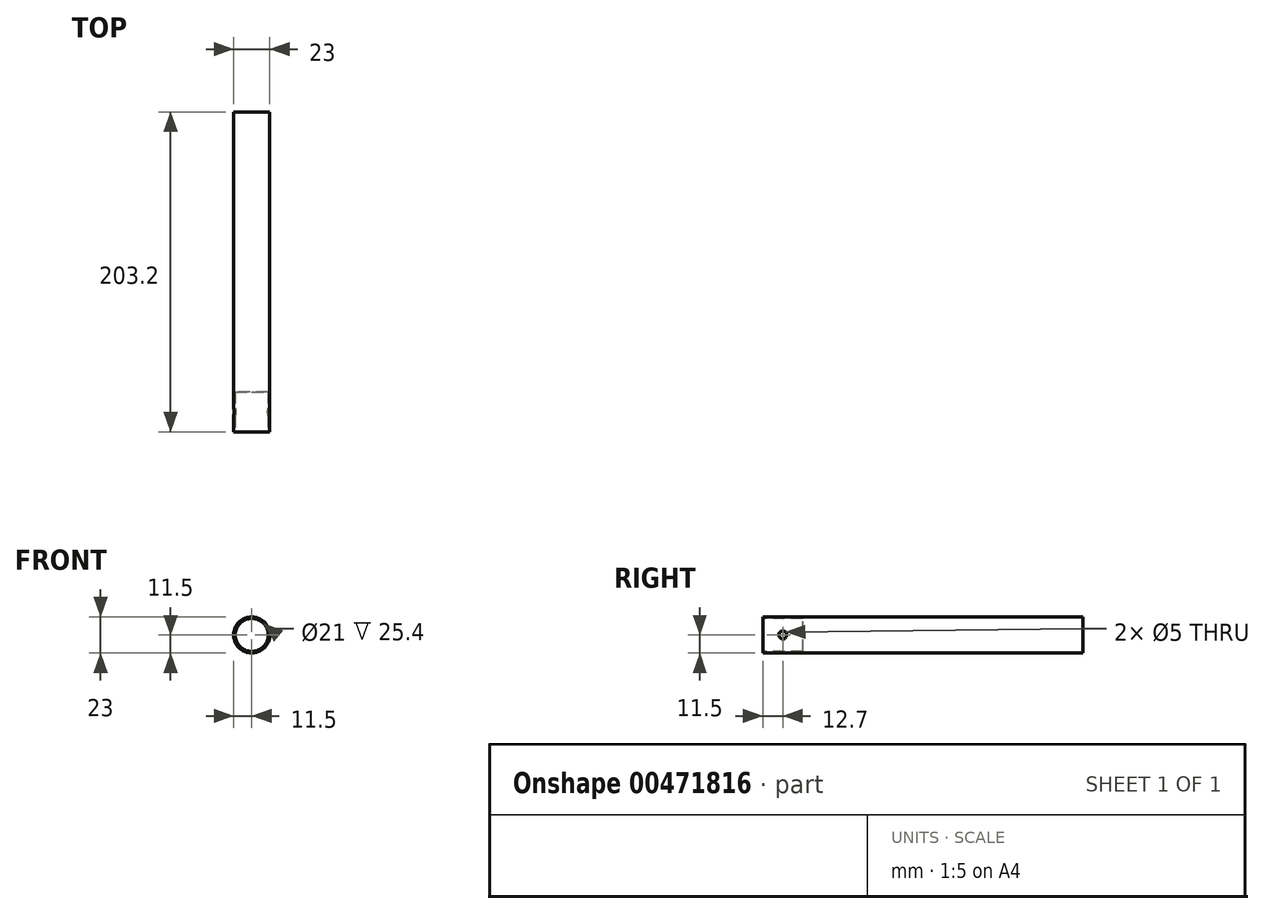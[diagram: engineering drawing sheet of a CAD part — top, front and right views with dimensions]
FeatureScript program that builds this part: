
annotation { "Feature Type Name" : "Feature", "Feature Type Description" : "" }
export const myFeature = defineFeature(function(context is Context, id is Id, definition is map)
    precondition{}
    {
        {
            var Q0;
            Q0=qCreatedBy(makeId("Front.planeOp"),FACE);
            var sketch = newSketch(context, id + "F0", { "sketchPlane" : qUnion([Q0])});
            skCircle(sketch, "E0", {"center": v(0, 0) * mm, "radius": 11.5 * mm});
            skCircle(sketch, "E1", {"center": v(0, 0) * mm, "radius": 10.5 * mm});
            skSolve(sketch);
        }
        {
            var Q0;
            Q0=makeQuery(id+"F0.imprint","IMPRINT",FACE,{"disambiguationData":[TD([[makeQuery(id+"F0.imprint","IMPRINT",EDGE,{"derivedFrom":sQuery(id+"F0.wireOp",EDGE,"E1")}),1.0]])]});
            var Q1;
            Q1=makeQuery(id+"F0.imprint","IMPRINT",FACE,{"disambiguationData":[TD([[makeQuery(id+"F0.imprint","IMPRINT",EDGE,{"derivedFrom":sQuery(id+"F0.wireOp",EDGE,"E0")}),1.0]])]});
            extrude(context, id + "F1", {"entities" : qUnion([Q0, Q1]), "oppositeDirection" : true, "depth" : 203.2 * mm});
        }
        {
            var Q0;
            Q0=makeQuery(id+"F0.imprint","IMPRINT",FACE,{"disambiguationData":[TD([[makeQuery(id+"F0.imprint","IMPRINT",EDGE,{"derivedFrom":sQuery(id+"F0.wireOp",EDGE,"E1")}),1.0]])]});
            extrude(context, id + "F2", {"entities" : qUnion([Q0]), "operationType" : NewBodyOperationType.REMOVE, "oppositeDirection" : true, "depth" : 25.4 * mm});
        }
        {
            var Q0;
            Q0=qCreatedBy(makeId("Right.planeOp"),FACE);
            var sketch = newSketch(context, id + "F3", { "sketchPlane" : qUnion([Q0])});
            skCircle(sketch, "E2", {"center": v(12.7, 0) * mm, "radius": 2.5 * mm});
            skSolve(sketch);
        }
        {
            var Q0;
            Q0=qSketchRegion(id+"F3",true);
            extrude(context, id + "F4", {"entities" : qUnion([Q0]), "operationType" : NewBodyOperationType.REMOVE, "endBound" : BoundingType.SYMMETRIC, "oppositeDirection" : true, "depth" : 25.4 * mm});
        }
    });
